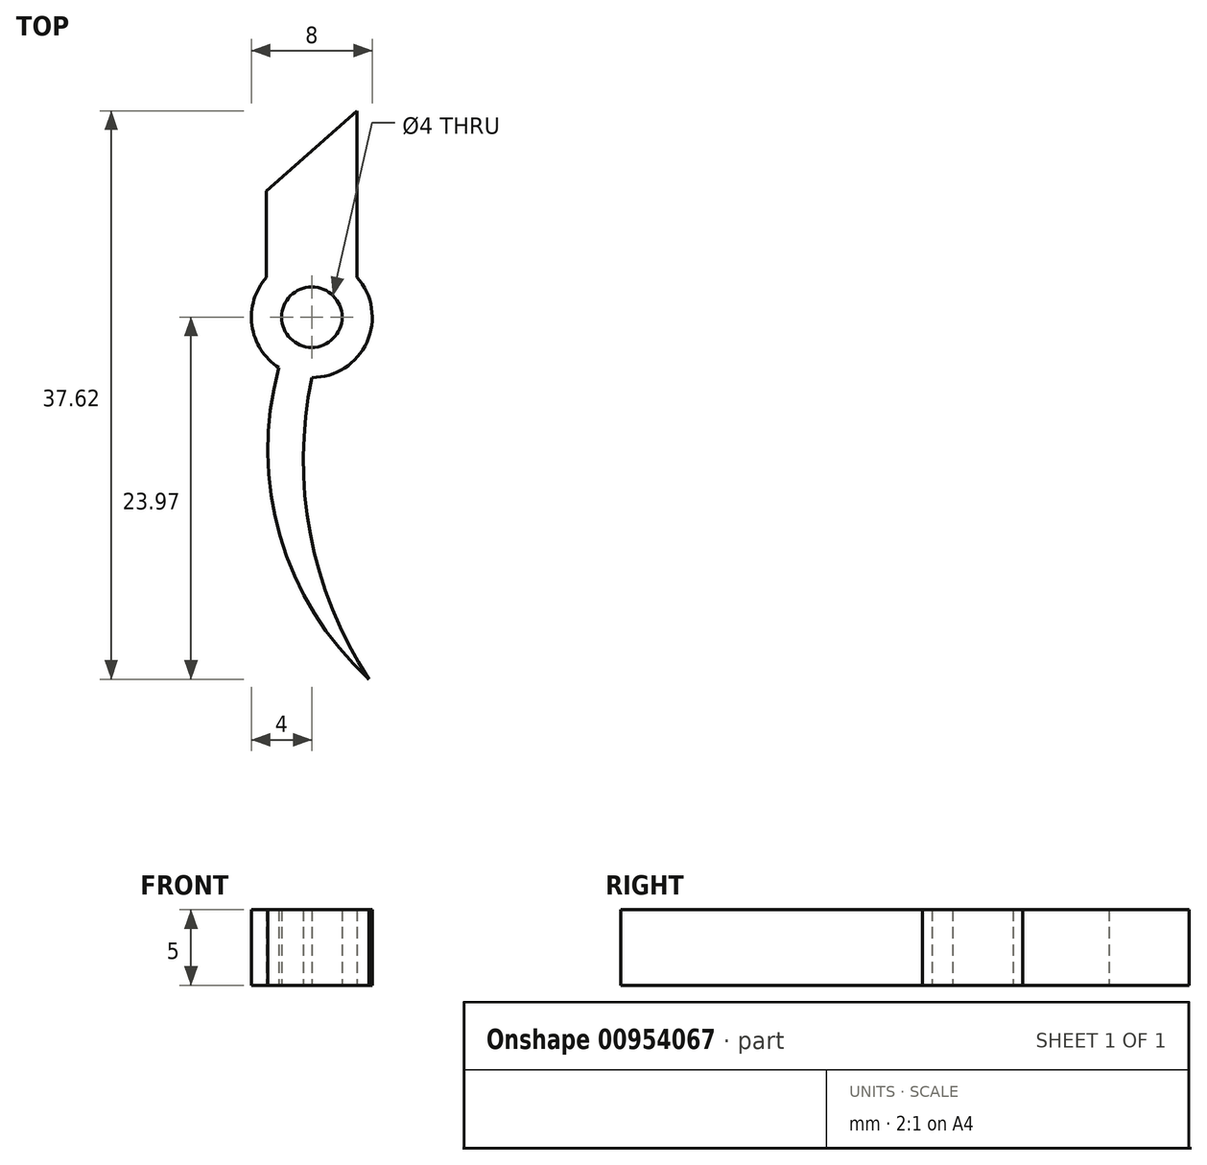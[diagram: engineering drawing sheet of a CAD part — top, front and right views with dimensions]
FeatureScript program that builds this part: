
annotation { "Feature Type Name" : "Feature", "Feature Type Description" : "" }
export const myFeature = defineFeature(function(context is Context, id is Id, definition is map)
    precondition{}
    {
        {
            var Q0;
            Q0=qCreatedBy(makeId("Top.planeOp"),FACE);
            var sketch = newSketch(context, id + "F0", { "sketchPlane" : qUnion([Q0])});
            skCircle(sketch, "E0", {"center": v(0, 0) * mm, "radius": 4 * mm});
            skLineSegment(sketch, "E1", {"start": v(-3, 2.65) * mm, "end": v(-3, 8.35) * mm});
            skLineSegment(sketch, "E2", {"start": v(3, 2.65) * mm, "end": v(3, 13.65) * mm});
            skLineSegment(sketch, "E3", {"start": v(3, 13.65) * mm, "end": v(-3, 8.35) * mm});
            skCircle(sketch, "E4", {"center": v(0, 0) * mm, "radius": 2 * mm});
            skArc(sketch, "E5", {"start": v(-2.18, -3.35) * mm, "mid": v(-2.1, -14.5) * mm, "end": v(3.78, -23.97) * mm});
            skArc(sketch, "E6", {"start": v(0, -4) * mm, "mid": v(-0.1, -14.36) * mm, "end": v(3.78, -23.97) * mm});
            skSolve(sketch);
        }
        {
            var Q0;
            {var subQ0=sQuery(id+"F0.wireOp",EDGE,"E1");Q0=makeQuery(id+"F0.imprint","IMPRINT",FACE,{"disambiguationData":[TD([[makeQuery(id+"F0.imprint","IMPRINT",EDGE,{"derivedFrom":subQ0}),-1.0]])]});}
            var Q1;
            Q1=makeQuery(id+"F0.imprint","IMPRINT",FACE,{"disambiguationData":[TD([[makeQuery(id+"F0.imprint","IMPRINT",EDGE,{"derivedFrom":sQuery(id+"F0.wireOp",EDGE,"E4")}),-1.0]])]});
            var Q2;
            {var subQ0=sQuery(id+"F0.wireOp",EDGE,"E5");Q2=makeQuery(id+"F0.imprint","IMPRINT",FACE,{"disambiguationData":[TD([[makeQuery(id+"F0.imprint","IMPRINT",EDGE,{"derivedFrom":subQ0}),1.0]])]});}
            extrude(context, id + "F1", {"entities" : qUnion([Q0, Q1, Q2]), "depth" : 5 * mm, "offsetDistance" : 25 * mm});
        }
    });
